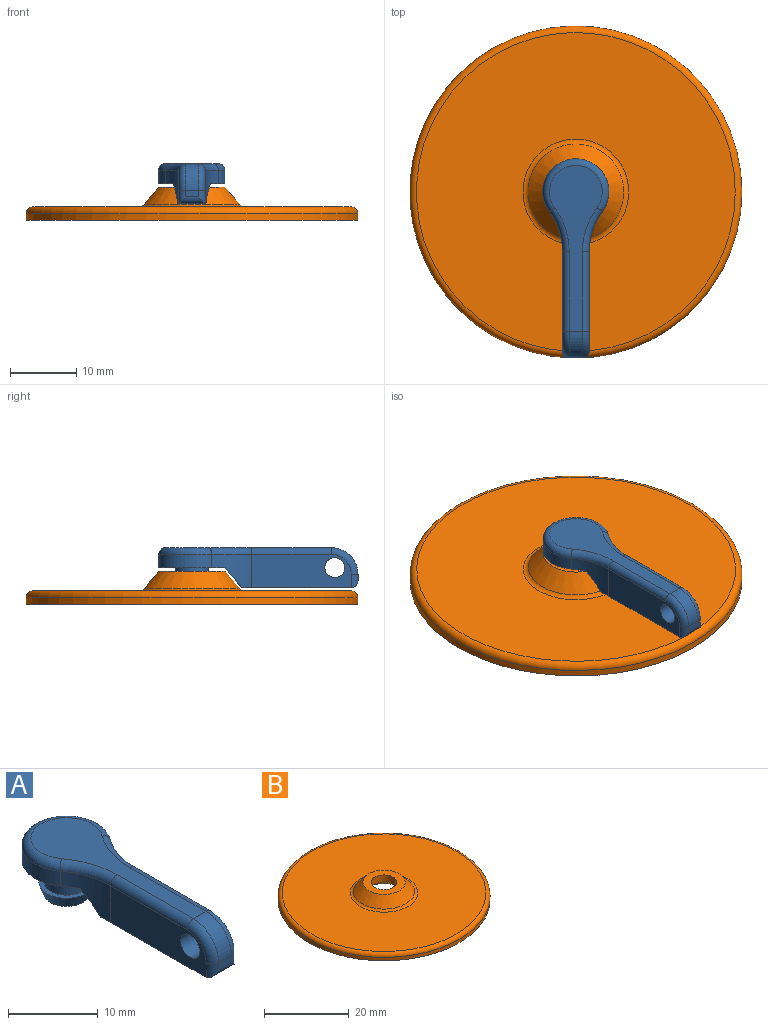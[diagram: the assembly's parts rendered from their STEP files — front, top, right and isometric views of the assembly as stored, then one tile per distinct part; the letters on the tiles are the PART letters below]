
ASSEMBLY  parts=2 mates=1
PART A: 26 faces, bbox 10.8x30.7x7.8 mm
  f0: cylinder r=2.5mm len=5mm, axis (0,0,1), area 47.1mm2, adj f3,f6
  f1: cone r=3.1mm half-angle=20deg, axis (0,0,1), area 28.4mm2, adj f2,f3
  f2: plane 5.11x5.11mm, normal (0,0,-1), area 20.5mm2, adj f1
  f3: plane 6.2x6.2mm, normal (0,0,1), area 10.6mm2, adj f0,f1
  f4: cylinder r=4.98mm len=9.97mm, axis (0,0,-1), area 44.1mm2, adj f6,f12,f13,f19
  f5: plane 24.98x7.97mm, normal (0,0,1), area 89.1mm2, adj f14,f16,f17,f19,f21,f23
  f6: plane 9.97x9.97mm, normal (0,0,-1), area 60.6mm2, adj f0,f4,f11,f12,f13
  f7: plane 15.03x5mm, normal (1,0,0), area 66.1mm2, adj f10,f12,f15,f23,f24,f25
  f8: plane 15.03x5mm, normal (-1,0,0), area 66.1mm2, adj f10,f13,f15,f16,f18,f20
  f9: plane 2x1mm, normal (0,-1,0), area 2mm2, adj f14,f20,f22,f24
  f10: plane 16.5x4.22mm, normal (0,0,-1), area 66.1mm2, adj f7,f8,f11,f12,f13,f22
  f11: plane 5.66x3mm, normal (0,0.77,-0.64), area 18.9mm2, adj f6,f10,f12,f13
  f12: cylinder r=10mm len=5.99mm, axis (0,0,-1), area 21.2mm2, adj f4,f6,f7,f10,f11,f21
  f13: cylinder r=10mm len=5.99mm, axis (0,0,-1), area 21.2mm2, adj f4,f6,f8,f10,f11,f17
  f14: cylinder r=4mm len=4mm, axis (-1,0,0), area 12.6mm2, adj f5,f9,f18,f25
  f15: cylinder r=1.5mm len=4mm, axis (1,0,0), area 37.7mm2, adj f7,f8
  f16: cylinder r=1mm len=12.03mm, axis (0,1,0), area 18.9mm2, adj f5,f8,f17,f18
  f17: torus R=11mm, axis (0,0,1), area 10.5mm2, adj f5,f13,f16,f19
  f18: torus R=3mm, axis (1,0,0), area 9mm2, adj f8,f14,f16,f20
  f19: torus R=3.98mm, axis (0,0,1), area 32.1mm2, adj f4,f5,f17,f21
  f20: cylinder r=1mm len=2mm, axis (0,0,-1), area 2.6mm2, adj f8,f9,f18,f22
  f21: torus R=11mm, axis (0,0,1), area 10.5mm2, adj f5,f12,f19,f23
  f22: cylinder r=1mm len=4mm, axis (1,0,0), area 5.1mm2, adj f9,f10,f20,f24
  f23: cylinder r=1mm len=12.03mm, axis (0,-1,0), area 18.9mm2, adj f5,f7,f21,f25
  f24: cylinder r=1mm len=2mm, axis (0,0,1), area 2.6mm2, adj f7,f9,f22,f25
  f25: torus R=3mm, axis (1,0,0), area 9mm2, adj f7,f14,f23,f24
PART B: 10 faces, bbox 54.1x54.1x5 mm
  f0: cylinder r=25mm len=50mm, axis (0,0,-1), area 157.1mm2, adj f2,f9
  f1: plane 48x48mm, normal (0,0,1), area 1610.2mm2, adj f8,f9
  f2: plane 50x50mm, normal (0,0,-1), area 1828mm2, adj f0,f5
  f3: cone r=7.5mm half-angle=40deg, axis (0,0,-1), area 132mm2, adj f4,f8
  f4: plane 9.97x9.97mm, normal (0,0,1), area 49.7mm2, adj f3,f7
  f5: cone r=5.97mm half-angle=40deg, axis (0,0,-1), area 130.6mm2, adj f2,f6
  f6: plane 8.1x8.1mm, normal (0,0,-1), area 23.3mm2, adj f5,f7
  f7: cylinder r=3mm len=6mm, axis (0,0,-1), area 37.7mm2, adj f4,f6
  f8: torus R=7.97mm, axis (0,0,1), area 41.4mm2, adj f1,f3
  f9: torus R=24mm, axis (0,0,1), area 243.2mm2, adj f0,f1
PLACE A t=(-1.32,7.05,6.83)mm
PLACE B t=(-1.32,7.05,6.83)mm
MATE revolute A.f0 <-> B.f0  axis (0,0,-1) through (-1.32,7.05,12.33)mm
